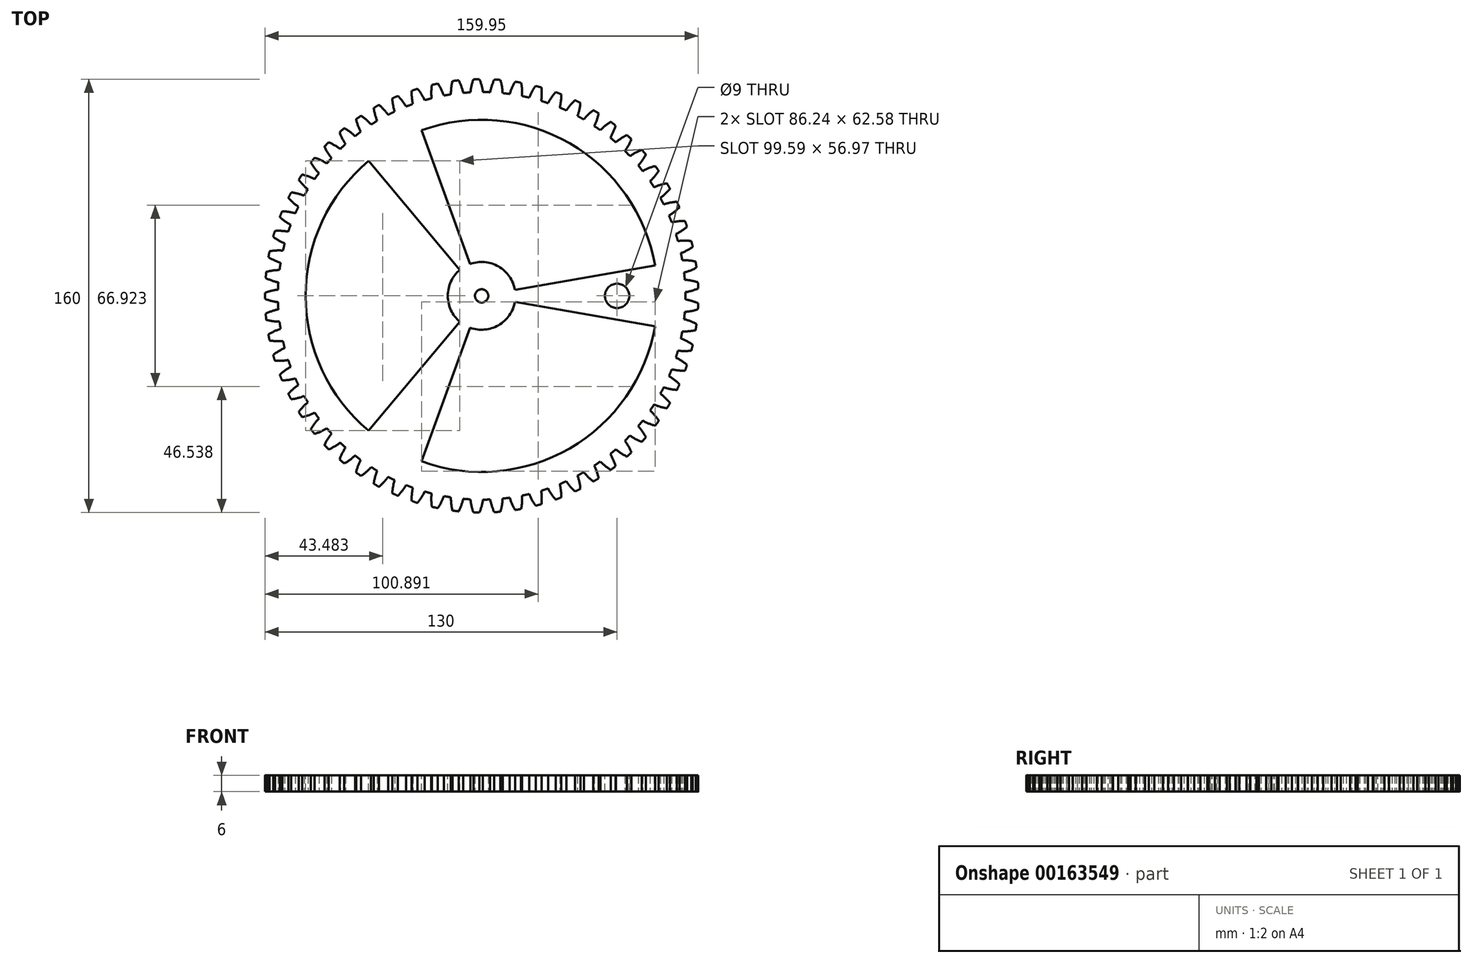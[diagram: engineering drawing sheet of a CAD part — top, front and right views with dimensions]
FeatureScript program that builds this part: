
annotation { "Feature Type Name" : "Feature", "Feature Type Description" : "" }
export const myFeature = defineFeature(function(context is Context, id is Id, definition is map)
    precondition{}
    {
        {
            var Q0;
            Q0=qCreatedBy(makeId("Top.planeOp"),FACE);
            var sketch = newSketch(context, id + "F0", { "sketchPlane" : qUnion([Q0])});
            skCircle(sketch, "E0", {"center": v(0, 0) * mm, "radius": 75.22 * mm, "construction": true});
            skCircle(sketch, "E1", {"center": v(0, 0) * mm, "radius": 77.61 * mm, "construction": true});
            skCircle(sketch, "E2", {"center": v(0, 0) * mm, "radius": 80 * mm, "construction": true});
            skLineSegment(sketch, "E3", {"start": v(0, 0) * mm, "end": v(0, 21.75) * mm, "construction": true});
            skLineSegment(sketch, "E4", {"start": v(0, 0) * mm, "end": v(-0.52, 21.72) * mm, "construction": true});
            skLineSegment(sketch, "E5", {"start": v(0, 77.61) * mm, "end": v(-10.54, 77.61) * mm, "construction": true});
            skLineSegment(sketch, "E6", {"start": v(0, 77.61) * mm, "end": v(-24.6, 71.02) * mm, "construction": true});
            skCircle(sketch, "E7", {"center": v(0, 77.61) * mm, "radius": 19.4 * mm, "construction": true});
            skCircle(sketch, "E8", {"center": v(-18.74, 72.6) * mm, "radius": 19.4 * mm, "construction": true});
            skArc(sketch, "E9", {"start": v(-37.48, 77.61) * mm, "mid": v(-38.1, 74.03) * mm, "end": v(-38.02, 70.39) * mm});
            skPoint(sketch, "E10.center", {"position": v(4.35, 4.65) * mm});
            skCircle(sketch, "E11", {"center": v(0, 0) * mm, "radius": 2.45 * mm});
            skArc(sketch, "E12", {"start": v(0.48, 75.22) * mm, "mid": v(-0.01, 77.65) * mm, "end": v(-0.8, 80) * mm});
            skArc(sketch, "E13.MirrorCS", {"start": v(-4.12, 75.11) * mm, "mid": v(-3.74, 77.56) * mm, "end": v(-3.06, 79.94) * mm});
            skArc(sketch, "E14", {"start": v(-0.8, 80) * mm, "mid": v(-1.93, 79.98) * mm, "end": v(-3.06, 79.94) * mm});
            skArc(sketch, "E15.1.0", {"start": v(-8.52, 79.54) * mm, "mid": v(-9.64, 79.42) * mm, "end": v(-10.76, 79.27) * mm});
            skArc(sketch, "E15.1.1", {"start": v(-6.78, 74.92) * mm, "mid": v(-7.5, 77.29) * mm, "end": v(-8.52, 79.54) * mm});
            skArc(sketch, "E15.1.2", {"start": v(-11.35, 74.36) * mm, "mid": v(-11.2, 76.84) * mm, "end": v(-10.76, 79.27) * mm});
            skArc(sketch, "E15.2.0", {"start": v(-16.16, 78.35) * mm, "mid": v(-17.26, 78.12) * mm, "end": v(-18.36, 77.86) * mm});
            skArc(sketch, "E15.2.1", {"start": v(-13.98, 73.91) * mm, "mid": v(-14.93, 76.2) * mm, "end": v(-16.16, 78.35) * mm});
            skArc(sketch, "E15.2.2", {"start": v(-18.47, 72.92) * mm, "mid": v(-18.57, 75.4) * mm, "end": v(-18.36, 77.86) * mm});
            skArc(sketch, "E15.3.0", {"start": v(-23.65, 76.42) * mm, "mid": v(-24.72, 76.08) * mm, "end": v(-25.79, 75.73) * mm});
            skArc(sketch, "E15.3.1", {"start": v(-21.05, 72.22) * mm, "mid": v(-22.21, 74.4) * mm, "end": v(-23.65, 76.42) * mm});
            skArc(sketch, "E15.3.2", {"start": v(-25.42, 70.8) * mm, "mid": v(-25.76, 73.25) * mm, "end": v(-25.79, 75.73) * mm});
            skArc(sketch, "E15.4.0", {"start": v(-30.91, 73.79) * mm, "mid": v(-31.95, 73.34) * mm, "end": v(-32.98, 72.89) * mm});
            skArc(sketch, "E15.4.1", {"start": v(-27.92, 69.85) * mm, "mid": v(-29.3, 71.91) * mm, "end": v(-30.91, 73.79) * mm});
            skArc(sketch, "E15.4.2", {"start": v(-32.14, 68.01) * mm, "mid": v(-32.71, 70.42) * mm, "end": v(-32.98, 72.89) * mm});
            skArc(sketch, "E15.5.0", {"start": v(-37.9, 70.46) * mm, "mid": v(-38.88, 69.92) * mm, "end": v(-39.86, 69.36) * mm});
            skArc(sketch, "E15.5.1", {"start": v(-34.53, 66.83) * mm, "mid": v(-36.1, 68.75) * mm, "end": v(-37.9, 70.46) * mm});
            skArc(sketch, "E15.5.2", {"start": v(-38.55, 64.6) * mm, "mid": v(-39.36, 66.94) * mm, "end": v(-39.86, 69.36) * mm});
            skArc(sketch, "E15.6.0", {"start": v(-44.51, 66.47) * mm, "mid": v(-45.45, 65.84) * mm, "end": v(-46.37, 65.2) * mm});
            skArc(sketch, "E15.6.1", {"start": v(-40.82, 63.19) * mm, "mid": v(-42.56, 64.95) * mm, "end": v(-44.51, 66.47) * mm});
            skArc(sketch, "E15.6.2", {"start": v(-44.6, 60.57) * mm, "mid": v(-45.63, 62.83) * mm, "end": v(-46.37, 65.2) * mm});
            skArc(sketch, "E15.7.0", {"start": v(-50.72, 61.86) * mm, "mid": v(-51.59, 61.15) * mm, "end": v(-52.44, 60.41) * mm});
            skArc(sketch, "E15.7.1", {"start": v(-46.73, 58.95) * mm, "mid": v(-48.63, 60.54) * mm, "end": v(-50.72, 61.86) * mm});
            skArc(sketch, "E15.7.2", {"start": v(-50.24, 55.99) * mm, "mid": v(-51.48, 58.13) * mm, "end": v(-52.44, 60.41) * mm});
            skArc(sketch, "E15.8.0", {"start": v(-56.46, 56.68) * mm, "mid": v(-57.25, 55.88) * mm, "end": v(-58.03, 55.07) * mm});
            skArc(sketch, "E15.8.1", {"start": v(-52.2, 54.17) * mm, "mid": v(-54.25, 55.56) * mm, "end": v(-56.46, 56.68) * mm});
            skArc(sketch, "E15.8.2", {"start": v(-55.41, 50.87) * mm, "mid": v(-56.85, 52.89) * mm, "end": v(-58.03, 55.07) * mm});
            skArc(sketch, "E15.9.0", {"start": v(-61.66, 50.97) * mm, "mid": v(-62.37, 50.1) * mm, "end": v(-63.07, 49.21) * mm});
            skArc(sketch, "E15.9.1", {"start": v(-57.18, 48.87) * mm, "mid": v(-59.36, 50.06) * mm, "end": v(-61.66, 50.97) * mm});
            skArc(sketch, "E15.9.2", {"start": v(-60.06, 45.29) * mm, "mid": v(-61.7, 47.15) * mm, "end": v(-63.07, 49.21) * mm});
            skArc(sketch, "E15.10.0", {"start": v(-66.3, 44.78) * mm, "mid": v(-66.92, 43.84) * mm, "end": v(-67.53, 42.9) * mm});
            skArc(sketch, "E15.10.1", {"start": v(-61.63, 43.13) * mm, "mid": v(-63.91, 44.1) * mm, "end": v(-66.3, 44.78) * mm});
            skArc(sketch, "E15.10.2", {"start": v(-64.15, 39.28) * mm, "mid": v(-65.96, 40.98) * mm, "end": v(-67.53, 42.9) * mm});
            skArc(sketch, "E15.11.0", {"start": v(-70.3, 38.17) * mm, "mid": v(-70.84, 37.18) * mm, "end": v(-71.35, 36.18) * mm});
            skArc(sketch, "E15.11.1", {"start": v(-65.5, 36.98) * mm, "mid": v(-67.87, 37.73) * mm, "end": v(-70.3, 38.17) * mm});
            skArc(sketch, "E15.11.2", {"start": v(-67.64, 32.9) * mm, "mid": v(-69.6, 34.42) * mm, "end": v(-71.35, 36.18) * mm});
            skArc(sketch, "E15.12.0", {"start": v(-73.66, 31.2) * mm, "mid": v(-74.1, 30.17) * mm, "end": v(-74.51, 29.12) * mm});
            skArc(sketch, "E15.12.1", {"start": v(-68.77, 30.48) * mm, "mid": v(-71.2, 31) * mm, "end": v(-73.66, 31.2) * mm});
            skArc(sketch, "E15.12.2", {"start": v(-70.5, 26.22) * mm, "mid": v(-72.6, 27.54) * mm, "end": v(-74.51, 29.12) * mm});
            skArc(sketch, "E15.13.0", {"start": v(-76.33, 23.95) * mm, "mid": v(-76.66, 22.88) * mm, "end": v(-76.97, 21.8) * mm});
            skArc(sketch, "E15.13.1", {"start": v(-71.4, 23.7) * mm, "mid": v(-73.85, 23.99) * mm, "end": v(-76.33, 23.95) * mm});
            skArc(sketch, "E15.13.2", {"start": v(-72.7, 19.3) * mm, "mid": v(-74.92, 20.4) * mm, "end": v(-76.97, 21.8) * mm});
            skArc(sketch, "E15.14.0", {"start": v(-78.29, 16.47) * mm, "mid": v(-78.5, 15.37) * mm, "end": v(-78.72, 14.26) * mm});
            skArc(sketch, "E15.14.1", {"start": v(-73.35, 16.7) * mm, "mid": v(-75.82, 16.75) * mm, "end": v(-78.29, 16.47) * mm});
            skArc(sketch, "E15.14.2", {"start": v(-74.23, 12.19) * mm, "mid": v(-76.54, 13.08) * mm, "end": v(-78.72, 14.26) * mm});
            skArc(sketch, "E15.15.0", {"start": v(-79.51, 8.84) * mm, "mid": v(-79.63, 7.72) * mm, "end": v(-79.73, 6.6) * mm});
            skArc(sketch, "E15.15.1", {"start": v(-74.62, 9.55) * mm, "mid": v(-77.09, 9.35) * mm, "end": v(-79.51, 8.84) * mm});
            skArc(sketch, "E15.15.2", {"start": v(-75.06, 4.97) * mm, "mid": v(-77.45, 5.63) * mm, "end": v(-79.73, 6.6) * mm});
            skArc(sketch, "E15.16.0", {"start": v(-80, 1.13) * mm, "mid": v(-80, 0) * mm, "end": v(-80, -1.13) * mm});
            skArc(sketch, "E15.16.1", {"start": v(-75.19, 2.3) * mm, "mid": v(-77.63, 1.87) * mm, "end": v(-80, 1.13) * mm});
            skArc(sketch, "E15.16.2", {"start": v(-75.19, -2.3) * mm, "mid": v(-77.63, -1.87) * mm, "end": v(-80, -1.13) * mm});
            skArc(sketch, "E15.17.0", {"start": v(-79.73, -6.6) * mm, "mid": v(-79.63, -7.72) * mm, "end": v(-79.51, -8.84) * mm});
            skArc(sketch, "E15.17.1", {"start": v(-75.06, -4.97) * mm, "mid": v(-77.45, -5.63) * mm, "end": v(-79.73, -6.6) * mm});
            skArc(sketch, "E15.17.2", {"start": v(-74.62, -9.55) * mm, "mid": v(-77.09, -9.35) * mm, "end": v(-79.51, -8.84) * mm});
            skArc(sketch, "E15.18.0", {"start": v(-78.72, -14.26) * mm, "mid": v(-78.5, -15.37) * mm, "end": v(-78.29, -16.47) * mm});
            skArc(sketch, "E15.18.1", {"start": v(-74.23, -12.19) * mm, "mid": v(-76.54, -13.08) * mm, "end": v(-78.72, -14.26) * mm});
            skArc(sketch, "E15.18.2", {"start": v(-73.35, -16.7) * mm, "mid": v(-75.82, -16.75) * mm, "end": v(-78.29, -16.47) * mm});
            skArc(sketch, "E15.19.0", {"start": v(-76.97, -21.8) * mm, "mid": v(-76.66, -22.88) * mm, "end": v(-76.33, -23.95) * mm});
            skArc(sketch, "E15.19.1", {"start": v(-72.7, -19.3) * mm, "mid": v(-74.92, -20.4) * mm, "end": v(-76.97, -21.8) * mm});
            skArc(sketch, "E15.19.2", {"start": v(-71.4, -23.7) * mm, "mid": v(-73.85, -23.99) * mm, "end": v(-76.33, -23.95) * mm});
            skArc(sketch, "E15.20.0", {"start": v(-74.51, -29.12) * mm, "mid": v(-74.1, -30.17) * mm, "end": v(-73.66, -31.2) * mm});
            skArc(sketch, "E15.20.1", {"start": v(-70.5, -26.22) * mm, "mid": v(-72.6, -27.54) * mm, "end": v(-74.51, -29.12) * mm});
            skArc(sketch, "E15.20.2", {"start": v(-68.77, -30.48) * mm, "mid": v(-71.2, -31) * mm, "end": v(-73.66, -31.2) * mm});
            skArc(sketch, "E15.21.0", {"start": v(-71.35, -36.18) * mm, "mid": v(-70.84, -37.18) * mm, "end": v(-70.3, -38.17) * mm});
            skArc(sketch, "E15.21.1", {"start": v(-67.64, -32.9) * mm, "mid": v(-69.6, -34.42) * mm, "end": v(-71.35, -36.18) * mm});
            skArc(sketch, "E15.21.2", {"start": v(-65.5, -36.98) * mm, "mid": v(-67.87, -37.73) * mm, "end": v(-70.3, -38.17) * mm});
            skArc(sketch, "E15.22.0", {"start": v(-67.53, -42.9) * mm, "mid": v(-66.92, -43.84) * mm, "end": v(-66.3, -44.78) * mm});
            skArc(sketch, "E15.22.1", {"start": v(-64.15, -39.28) * mm, "mid": v(-65.96, -40.98) * mm, "end": v(-67.53, -42.9) * mm});
            skArc(sketch, "E15.22.2", {"start": v(-61.63, -43.13) * mm, "mid": v(-63.91, -44.1) * mm, "end": v(-66.3, -44.78) * mm});
            skArc(sketch, "E15.23.0", {"start": v(-63.07, -49.21) * mm, "mid": v(-62.37, -50.1) * mm, "end": v(-61.66, -50.97) * mm});
            skArc(sketch, "E15.23.1", {"start": v(-60.06, -45.29) * mm, "mid": v(-61.7, -47.15) * mm, "end": v(-63.07, -49.21) * mm});
            skArc(sketch, "E15.23.2", {"start": v(-57.18, -48.87) * mm, "mid": v(-59.36, -50.06) * mm, "end": v(-61.66, -50.97) * mm});
            skArc(sketch, "E15.24.0", {"start": v(-58.03, -55.07) * mm, "mid": v(-57.25, -55.88) * mm, "end": v(-56.46, -56.68) * mm});
            skArc(sketch, "E15.24.1", {"start": v(-55.41, -50.87) * mm, "mid": v(-56.85, -52.89) * mm, "end": v(-58.03, -55.07) * mm});
            skArc(sketch, "E15.24.2", {"start": v(-52.2, -54.17) * mm, "mid": v(-54.25, -55.56) * mm, "end": v(-56.46, -56.68) * mm});
            skArc(sketch, "E15.25.0", {"start": v(-52.44, -60.41) * mm, "mid": v(-51.59, -61.15) * mm, "end": v(-50.72, -61.86) * mm});
            skArc(sketch, "E15.25.1", {"start": v(-50.24, -55.99) * mm, "mid": v(-51.48, -58.13) * mm, "end": v(-52.44, -60.41) * mm});
            skArc(sketch, "E15.25.2", {"start": v(-46.73, -58.95) * mm, "mid": v(-48.63, -60.54) * mm, "end": v(-50.72, -61.86) * mm});
            skArc(sketch, "E15.26.0", {"start": v(-46.37, -65.2) * mm, "mid": v(-45.45, -65.84) * mm, "end": v(-44.51, -66.47) * mm});
            skArc(sketch, "E15.26.1", {"start": v(-44.6, -60.57) * mm, "mid": v(-45.63, -62.83) * mm, "end": v(-46.37, -65.2) * mm});
            skArc(sketch, "E15.26.2", {"start": v(-40.82, -63.19) * mm, "mid": v(-42.56, -64.95) * mm, "end": v(-44.51, -66.47) * mm});
            skArc(sketch, "E15.27.0", {"start": v(-39.86, -69.36) * mm, "mid": v(-38.88, -69.92) * mm, "end": v(-37.9, -70.46) * mm});
            skArc(sketch, "E15.27.1", {"start": v(-38.55, -64.6) * mm, "mid": v(-39.36, -66.94) * mm, "end": v(-39.86, -69.36) * mm});
            skArc(sketch, "E15.27.2", {"start": v(-34.53, -66.83) * mm, "mid": v(-36.1, -68.75) * mm, "end": v(-37.9, -70.46) * mm});
            skArc(sketch, "E15.28.0", {"start": v(-32.98, -72.89) * mm, "mid": v(-31.95, -73.34) * mm, "end": v(-30.91, -73.79) * mm});
            skArc(sketch, "E15.28.1", {"start": v(-32.14, -68.01) * mm, "mid": v(-32.71, -70.42) * mm, "end": v(-32.98, -72.89) * mm});
            skArc(sketch, "E15.28.2", {"start": v(-27.92, -69.85) * mm, "mid": v(-29.3, -71.91) * mm, "end": v(-30.91, -73.79) * mm});
            skArc(sketch, "E15.29.0", {"start": v(-25.79, -75.73) * mm, "mid": v(-24.72, -76.08) * mm, "end": v(-23.65, -76.42) * mm});
            skArc(sketch, "E15.29.1", {"start": v(-25.42, -70.8) * mm, "mid": v(-25.76, -73.25) * mm, "end": v(-25.79, -75.73) * mm});
            skArc(sketch, "E15.29.2", {"start": v(-21.05, -72.22) * mm, "mid": v(-22.21, -74.4) * mm, "end": v(-23.65, -76.42) * mm});
            skArc(sketch, "E15.30.0", {"start": v(-18.36, -77.86) * mm, "mid": v(-17.26, -78.12) * mm, "end": v(-16.16, -78.35) * mm});
            skArc(sketch, "E15.30.1", {"start": v(-18.47, -72.92) * mm, "mid": v(-18.57, -75.4) * mm, "end": v(-18.36, -77.86) * mm});
            skArc(sketch, "E15.30.2", {"start": v(-13.98, -73.91) * mm, "mid": v(-14.93, -76.2) * mm, "end": v(-16.16, -78.35) * mm});
            skArc(sketch, "E15.31.0", {"start": v(-10.76, -79.27) * mm, "mid": v(-9.64, -79.42) * mm, "end": v(-8.52, -79.54) * mm});
            skArc(sketch, "E15.31.1", {"start": v(-11.35, -74.36) * mm, "mid": v(-11.2, -76.84) * mm, "end": v(-10.76, -79.27) * mm});
            skArc(sketch, "E15.31.2", {"start": v(-6.78, -74.92) * mm, "mid": v(-7.5, -77.29) * mm, "end": v(-8.52, -79.54) * mm});
            skArc(sketch, "E15.32.0", {"start": v(-3.06, -79.94) * mm, "mid": v(-1.93, -79.98) * mm, "end": v(-0.8, -80) * mm});
            skArc(sketch, "E15.32.1", {"start": v(-4.12, -75.11) * mm, "mid": v(-3.74, -77.56) * mm, "end": v(-3.06, -79.94) * mm});
            skArc(sketch, "E15.32.2", {"start": v(0.48, -75.22) * mm, "mid": v(-0.01, -77.65) * mm, "end": v(-0.8, -80) * mm});
            skArc(sketch, "E15.33.0", {"start": v(4.67, -79.86) * mm, "mid": v(5.8, -79.79) * mm, "end": v(6.92, -79.7) * mm});
            skArc(sketch, "E15.33.1", {"start": v(3.15, -75.16) * mm, "mid": v(3.76, -77.56) * mm, "end": v(4.67, -79.86) * mm});
            skArc(sketch, "E15.33.2", {"start": v(7.74, -74.82) * mm, "mid": v(7.48, -77.29) * mm, "end": v(6.92, -79.7) * mm});
            skArc(sketch, "E15.34.0", {"start": v(12.36, -79.04) * mm, "mid": v(13.47, -78.86) * mm, "end": v(14.58, -78.66) * mm});
            skArc(sketch, "E15.34.1", {"start": v(10.4, -74.5) * mm, "mid": v(11.23, -76.83) * mm, "end": v(12.36, -79.04) * mm});
            skArc(sketch, "E15.34.2", {"start": v(14.93, -73.73) * mm, "mid": v(14.9, -76.2) * mm, "end": v(14.58, -78.66) * mm});
            skArc(sketch, "E15.35.0", {"start": v(19.93, -77.48) * mm, "mid": v(21.02, -77.2) * mm, "end": v(22.1, -76.89) * mm});
            skArc(sketch, "E15.35.1", {"start": v(17.53, -73.15) * mm, "mid": v(18.6, -75.4) * mm, "end": v(19.93, -77.48) * mm});
            skArc(sketch, "E15.35.2", {"start": v(21.97, -71.94) * mm, "mid": v(22.2, -74.41) * mm, "end": v(22.1, -76.89) * mm});
            skArc(sketch, "E15.36.0", {"start": v(27.31, -75.2) * mm, "mid": v(28.37, -74.8) * mm, "end": v(29.42, -74.4) * mm});
            skArc(sketch, "E15.36.1", {"start": v(24.51, -71.12) * mm, "mid": v(25.78, -73.25) * mm, "end": v(27.31, -75.2) * mm});
            skArc(sketch, "E15.36.2", {"start": v(28.81, -69.49) * mm, "mid": v(29.27, -71.92) * mm, "end": v(29.42, -74.4) * mm});
            skArc(sketch, "E15.37.0", {"start": v(34.44, -72.2) * mm, "mid": v(35.46, -71.71) * mm, "end": v(36.46, -71.2) * mm});
            skArc(sketch, "E15.37.1", {"start": v(31.26, -68.42) * mm, "mid": v(32.73, -70.41) * mm, "end": v(34.44, -72.2) * mm});
            skArc(sketch, "E15.37.2", {"start": v(35.38, -66.38) * mm, "mid": v(36.08, -68.76) * mm, "end": v(36.46, -71.2) * mm});
            skArc(sketch, "E15.38.0", {"start": v(41.25, -68.54) * mm, "mid": v(42.21, -67.96) * mm, "end": v(43.16, -67.36) * mm});
            skArc(sketch, "E15.38.1", {"start": v(37.72, -65.08) * mm, "mid": v(39.37, -66.93) * mm, "end": v(41.25, -68.54) * mm});
            skArc(sketch, "E15.38.2", {"start": v(41.63, -62.66) * mm, "mid": v(42.54, -64.96) * mm, "end": v(43.16, -67.36) * mm});
            skArc(sketch, "E15.39.0", {"start": v(47.67, -64.24) * mm, "mid": v(48.57, -63.57) * mm, "end": v(49.46, -62.88) * mm});
            skArc(sketch, "E15.39.1", {"start": v(43.82, -61.14) * mm, "mid": v(45.65, -62.81) * mm, "end": v(47.67, -64.24) * mm});
            skArc(sketch, "E15.39.2", {"start": v(47.48, -58.35) * mm, "mid": v(48.62, -60.55) * mm, "end": v(49.46, -62.88) * mm});
            skArc(sketch, "E15.40.0", {"start": v(53.65, -59.34) * mm, "mid": v(54.48, -58.58) * mm, "end": v(55.3, -57.8) * mm});
            skArc(sketch, "E15.40.1", {"start": v(49.52, -56.62) * mm, "mid": v(51.5, -58.12) * mm, "end": v(53.65, -59.34) * mm});
            skArc(sketch, "E15.40.2", {"start": v(52.89, -53.5) * mm, "mid": v(54.23, -55.57) * mm, "end": v(55.3, -57.8) * mm});
            skArc(sketch, "E15.41.0", {"start": v(59.13, -53.89) * mm, "mid": v(59.88, -53.05) * mm, "end": v(60.62, -52.2) * mm});
            skArc(sketch, "E15.41.1", {"start": v(54.75, -51.58) * mm, "mid": v(56.87, -52.87) * mm, "end": v(59.13, -53.89) * mm});
            skArc(sketch, "E15.41.2", {"start": v(57.8, -48.14) * mm, "mid": v(59.34, -50.08) * mm, "end": v(60.62, -52.2) * mm});
            skArc(sketch, "E15.42.0", {"start": v(64.05, -47.93) * mm, "mid": v(64.72, -47.02) * mm, "end": v(65.38, -46.1) * mm});
            skArc(sketch, "E15.42.1", {"start": v(59.48, -46.05) * mm, "mid": v(61.7, -47.14) * mm, "end": v(64.05, -47.93) * mm});
            skArc(sketch, "E15.42.2", {"start": v(62.18, -42.33) * mm, "mid": v(63.9, -44.12) * mm, "end": v(65.38, -46.1) * mm});
            skArc(sketch, "E15.43.0", {"start": v(68.38, -41.52) * mm, "mid": v(68.96, -40.56) * mm, "end": v(69.52, -39.58) * mm});
            skArc(sketch, "E15.43.1", {"start": v(63.64, -40.1) * mm, "mid": v(65.97, -40.96) * mm, "end": v(68.38, -41.52) * mm});
            skArc(sketch, "E15.43.2", {"start": v(65.98, -36.14) * mm, "mid": v(67.86, -37.75) * mm, "end": v(69.52, -39.58) * mm});
            skArc(sketch, "E15.44.0", {"start": v(72.07, -34.73) * mm, "mid": v(72.55, -33.71) * mm, "end": v(73.02, -32.69) * mm});
            skArc(sketch, "E15.44.1", {"start": v(67.22, -33.77) * mm, "mid": v(69.61, -34.4) * mm, "end": v(72.07, -34.73) * mm});
            skArc(sketch, "E15.44.2", {"start": v(69.16, -29.6) * mm, "mid": v(71.19, -31.02) * mm, "end": v(73.02, -32.69) * mm});
            skArc(sketch, "E15.45.0", {"start": v(75.08, -27.61) * mm, "mid": v(75.46, -26.55) * mm, "end": v(75.83, -25.49) * mm});
            skArc(sketch, "E15.45.1", {"start": v(70.16, -27.12) * mm, "mid": v(72.6, -27.53) * mm, "end": v(75.08, -27.61) * mm});
            skArc(sketch, "E15.45.2", {"start": v(71.69, -22.79) * mm, "mid": v(73.85, -24) * mm, "end": v(75.83, -25.49) * mm});
            skArc(sketch, "E15.46.0", {"start": v(77.4, -20.24) * mm, "mid": v(77.68, -19.15) * mm, "end": v(77.94, -18.05) * mm});
            skArc(sketch, "E15.46.1", {"start": v(72.45, -20.23) * mm, "mid": v(74.93, -20.39) * mm, "end": v(77.4, -20.24) * mm});
            skArc(sketch, "E15.46.2", {"start": v(73.55, -15.76) * mm, "mid": v(75.82, -16.77) * mm, "end": v(77.94, -18.05) * mm});
            skArc(sketch, "E15.47.0", {"start": v(79, -12.67) * mm, "mid": v(79.16, -11.56) * mm, "end": v(79.32, -10.44) * mm});
            skArc(sketch, "E15.47.1", {"start": v(74.07, -13.14) * mm, "mid": v(76.54, -13.06) * mm, "end": v(79, -12.67) * mm});
            skArc(sketch, "E15.47.2", {"start": v(74.73, -8.59) * mm, "mid": v(77.08, -9.37) * mm, "end": v(79.32, -10.44) * mm});
            skArc(sketch, "E16.4.48.0", {"start": v(74.99, -5.93) * mm, "mid": v(77.45, -5.61) * mm, "end": v(79.84, -4.99) * mm});
            skArc(sketch, "E16.8.48.0", {"start": v(75.21, -1.34) * mm, "mid": v(77.63, -1.89) * mm, "end": v(79.95, -2.74) * mm});
            skArc(sketch, "E16.10.48.0", {"start": v(79.84, -4.99) * mm, "mid": v(79.9, -3.87) * mm, "end": v(79.95, -2.74) * mm});
            skArc(sketch, "E16.4.49.0", {"start": v(75.21, 1.34) * mm, "mid": v(77.63, 1.89) * mm, "end": v(79.95, 2.74) * mm});
            skArc(sketch, "E16.8.49.0", {"start": v(74.99, 5.93) * mm, "mid": v(77.45, 5.61) * mm, "end": v(79.84, 4.99) * mm});
            skArc(sketch, "E16.10.49.0", {"start": v(79.95, 2.74) * mm, "mid": v(79.9, 3.87) * mm, "end": v(79.84, 4.99) * mm});
            skArc(sketch, "E17", {"start": v(3.15, 75.16) * mm, "mid": v(1.82, 75.2) * mm, "end": v(0.48, 75.22) * mm});
            skArc(sketch, "E18.1.0", {"start": v(-4.12, 75.11) * mm, "mid": v(-5.45, 75.03) * mm, "end": v(-6.78, 74.92) * mm});
            skArc(sketch, "E18.2.0", {"start": v(-11.35, 74.36) * mm, "mid": v(-12.66, 74.15) * mm, "end": v(-13.98, 73.91) * mm});
            skArc(sketch, "E18.3.0", {"start": v(-18.47, 72.92) * mm, "mid": v(-19.76, 72.58) * mm, "end": v(-21.05, 72.22) * mm});
            skArc(sketch, "E18.4.0", {"start": v(-25.42, 70.8) * mm, "mid": v(-26.67, 70.34) * mm, "end": v(-27.92, 69.85) * mm});
            skArc(sketch, "E18.5.0", {"start": v(-32.14, 68.01) * mm, "mid": v(-33.34, 67.43) * mm, "end": v(-34.53, 66.83) * mm});
            skArc(sketch, "E18.6.0", {"start": v(-38.55, 64.6) * mm, "mid": v(-39.7, 63.9) * mm, "end": v(-40.82, 63.19) * mm});
            skArc(sketch, "E18.7.0", {"start": v(-44.6, 60.57) * mm, "mid": v(-45.67, 59.77) * mm, "end": v(-46.73, 58.95) * mm});
            skArc(sketch, "E18.8.0", {"start": v(-50.24, 55.99) * mm, "mid": v(-51.23, 55.08) * mm, "end": v(-52.2, 54.17) * mm});
            skArc(sketch, "E18.9.0", {"start": v(-55.41, 50.87) * mm, "mid": v(-56.3, 49.88) * mm, "end": v(-57.18, 48.87) * mm});
            skArc(sketch, "E18.10.0", {"start": v(-60.06, 45.29) * mm, "mid": v(-60.86, 44.22) * mm, "end": v(-61.63, 43.13) * mm});
            skArc(sketch, "E18.11.0", {"start": v(-64.15, 39.28) * mm, "mid": v(-64.84, 38.14) * mm, "end": v(-65.5, 36.98) * mm});
            skArc(sketch, "E18.12.0", {"start": v(-67.64, 32.9) * mm, "mid": v(-68.22, 31.7) * mm, "end": v(-68.77, 30.48) * mm});
            skArc(sketch, "E18.13.0", {"start": v(-70.5, 26.22) * mm, "mid": v(-70.96, 24.97) * mm, "end": v(-71.4, 23.7) * mm});
            skArc(sketch, "E18.14.0", {"start": v(-72.7, 19.3) * mm, "mid": v(-73.04, 18) * mm, "end": v(-73.35, 16.7) * mm});
            skArc(sketch, "E18.15.0", {"start": v(-74.23, 12.19) * mm, "mid": v(-74.43, 10.87) * mm, "end": v(-74.62, 9.55) * mm});
            skArc(sketch, "E18.16.0", {"start": v(-75.06, 4.97) * mm, "mid": v(-75.14, 3.63) * mm, "end": v(-75.19, 2.3) * mm});
            skArc(sketch, "E18.17.0", {"start": v(-75.19, -2.3) * mm, "mid": v(-75.14, -3.63) * mm, "end": v(-75.06, -4.97) * mm});
            skArc(sketch, "E18.18.0", {"start": v(-74.62, -9.55) * mm, "mid": v(-74.43, -10.87) * mm, "end": v(-74.23, -12.19) * mm});
            skArc(sketch, "E18.19.0", {"start": v(-73.35, -16.7) * mm, "mid": v(-73.04, -18) * mm, "end": v(-72.7, -19.3) * mm});
            skArc(sketch, "E18.20.0", {"start": v(-71.4, -23.7) * mm, "mid": v(-70.96, -24.97) * mm, "end": v(-70.5, -26.22) * mm});
            skArc(sketch, "E18.21.0", {"start": v(-68.77, -30.48) * mm, "mid": v(-68.22, -31.7) * mm, "end": v(-67.64, -32.9) * mm});
            skArc(sketch, "E18.22.0", {"start": v(-65.5, -36.98) * mm, "mid": v(-64.84, -38.14) * mm, "end": v(-64.15, -39.28) * mm});
            skArc(sketch, "E18.23.0", {"start": v(-61.63, -43.13) * mm, "mid": v(-60.86, -44.22) * mm, "end": v(-60.06, -45.29) * mm});
            skArc(sketch, "E18.24.0", {"start": v(-57.18, -48.87) * mm, "mid": v(-56.3, -49.88) * mm, "end": v(-55.41, -50.87) * mm});
            skArc(sketch, "E18.25.0", {"start": v(-52.2, -54.17) * mm, "mid": v(-51.23, -55.08) * mm, "end": v(-50.24, -55.99) * mm});
            skArc(sketch, "E18.26.0", {"start": v(-46.73, -58.95) * mm, "mid": v(-45.67, -59.77) * mm, "end": v(-44.6, -60.57) * mm});
            skArc(sketch, "E18.27.0", {"start": v(-40.82, -63.19) * mm, "mid": v(-39.7, -63.9) * mm, "end": v(-38.55, -64.6) * mm});
            skArc(sketch, "E18.28.0", {"start": v(-34.53, -66.83) * mm, "mid": v(-33.34, -67.43) * mm, "end": v(-32.14, -68.01) * mm});
            skArc(sketch, "E18.29.0", {"start": v(-27.92, -69.85) * mm, "mid": v(-26.67, -70.34) * mm, "end": v(-25.42, -70.8) * mm});
            skArc(sketch, "E18.30.0", {"start": v(-21.05, -72.22) * mm, "mid": v(-19.76, -72.58) * mm, "end": v(-18.47, -72.92) * mm});
            skArc(sketch, "E18.31.0", {"start": v(-13.98, -73.91) * mm, "mid": v(-12.66, -74.15) * mm, "end": v(-11.35, -74.36) * mm});
            skArc(sketch, "E18.32.0", {"start": v(-6.78, -74.92) * mm, "mid": v(-5.45, -75.03) * mm, "end": v(-4.12, -75.11) * mm});
            skArc(sketch, "E18.33.0", {"start": v(0.48, -75.22) * mm, "mid": v(1.82, -75.2) * mm, "end": v(3.15, -75.16) * mm});
            skArc(sketch, "E18.34.0", {"start": v(7.74, -74.82) * mm, "mid": v(9.07, -74.68) * mm, "end": v(10.4, -74.5) * mm});
            skArc(sketch, "E18.35.0", {"start": v(14.93, -73.73) * mm, "mid": v(16.23, -73.45) * mm, "end": v(17.53, -73.15) * mm});
            skArc(sketch, "E18.36.0", {"start": v(21.97, -71.94) * mm, "mid": v(23.25, -71.54) * mm, "end": v(24.51, -71.12) * mm});
            skArc(sketch, "E18.37.0", {"start": v(28.81, -69.49) * mm, "mid": v(30.04, -68.96) * mm, "end": v(31.26, -68.42) * mm});
            skArc(sketch, "E18.38.0", {"start": v(35.38, -66.38) * mm, "mid": v(36.56, -65.74) * mm, "end": v(37.72, -65.08) * mm});
            skArc(sketch, "E18.39.0", {"start": v(41.63, -62.66) * mm, "mid": v(42.73, -61.9) * mm, "end": v(43.82, -61.14) * mm});
            skArc(sketch, "E18.40.0", {"start": v(47.48, -58.35) * mm, "mid": v(48.5, -57.5) * mm, "end": v(49.52, -56.62) * mm});
            skArc(sketch, "E18.41.0", {"start": v(52.89, -53.5) * mm, "mid": v(53.83, -52.54) * mm, "end": v(54.75, -51.58) * mm});
            skArc(sketch, "E18.42.0", {"start": v(57.8, -48.14) * mm, "mid": v(58.65, -47.1) * mm, "end": v(59.48, -46.05) * mm});
            skArc(sketch, "E18.43.0", {"start": v(62.18, -42.33) * mm, "mid": v(62.92, -41.22) * mm, "end": v(63.64, -40.1) * mm});
            skArc(sketch, "E18.44.0", {"start": v(65.98, -36.14) * mm, "mid": v(66.6, -34.96) * mm, "end": v(67.22, -33.77) * mm});
            skArc(sketch, "E18.45.0", {"start": v(69.16, -29.6) * mm, "mid": v(69.67, -28.37) * mm, "end": v(70.16, -27.12) * mm});
            skArc(sketch, "E18.46.0", {"start": v(71.69, -22.79) * mm, "mid": v(72.08, -21.5) * mm, "end": v(72.45, -20.23) * mm});
            skArc(sketch, "E18.47.0", {"start": v(73.55, -15.76) * mm, "mid": v(73.82, -14.45) * mm, "end": v(74.07, -13.14) * mm});
            skArc(sketch, "E18.48.0", {"start": v(74.73, -8.59) * mm, "mid": v(74.87, -7.26) * mm, "end": v(74.99, -5.93) * mm});
            skArc(sketch, "E18.49.0", {"start": v(75.21, -1.34) * mm, "mid": v(75.22, 0) * mm, "end": v(75.21, 1.34) * mm});
            skArc(sketch, "E19.4.50.0", {"start": v(74.73, 8.59) * mm, "mid": v(77.08, 9.37) * mm, "end": v(79.32, 10.44) * mm});
            skArc(sketch, "E19.8.50.0", {"start": v(74.07, 13.14) * mm, "mid": v(76.54, 13.06) * mm, "end": v(79, 12.67) * mm});
            skArc(sketch, "E19.10.50.0", {"start": v(79.32, 10.44) * mm, "mid": v(79.16, 11.56) * mm, "end": v(79, 12.67) * mm});
            skArc(sketch, "E20.3.50.0", {"start": v(74.99, 5.93) * mm, "mid": v(74.87, 7.26) * mm, "end": v(74.73, 8.59) * mm});
            skArc(sketch, "E21.4.51.0", {"start": v(73.55, 15.76) * mm, "mid": v(75.82, 16.77) * mm, "end": v(77.94, 18.05) * mm});
            skArc(sketch, "E21.8.51.0", {"start": v(72.45, 20.23) * mm, "mid": v(74.93, 20.39) * mm, "end": v(77.4, 20.24) * mm});
            skArc(sketch, "E21.10.51.0", {"start": v(77.94, 18.05) * mm, "mid": v(77.68, 19.15) * mm, "end": v(77.4, 20.24) * mm});
            skArc(sketch, "E21.4.52.0", {"start": v(71.69, 22.79) * mm, "mid": v(73.85, 24) * mm, "end": v(75.83, 25.49) * mm});
            skArc(sketch, "E21.8.52.0", {"start": v(70.16, 27.12) * mm, "mid": v(72.6, 27.53) * mm, "end": v(75.08, 27.61) * mm});
            skArc(sketch, "E21.10.52.0", {"start": v(75.83, 25.49) * mm, "mid": v(75.46, 26.55) * mm, "end": v(75.08, 27.61) * mm});
            skArc(sketch, "E21.4.53.0", {"start": v(69.16, 29.6) * mm, "mid": v(71.19, 31.02) * mm, "end": v(73.02, 32.69) * mm});
            skArc(sketch, "E21.8.53.0", {"start": v(67.22, 33.77) * mm, "mid": v(69.61, 34.4) * mm, "end": v(72.07, 34.73) * mm});
            skArc(sketch, "E21.10.53.0", {"start": v(73.02, 32.69) * mm, "mid": v(72.55, 33.71) * mm, "end": v(72.07, 34.73) * mm});
            skArc(sketch, "E21.4.54.0", {"start": v(65.98, 36.14) * mm, "mid": v(67.86, 37.75) * mm, "end": v(69.52, 39.58) * mm});
            skArc(sketch, "E21.8.54.0", {"start": v(63.64, 40.1) * mm, "mid": v(65.97, 40.96) * mm, "end": v(68.38, 41.52) * mm});
            skArc(sketch, "E21.10.54.0", {"start": v(69.52, 39.58) * mm, "mid": v(68.96, 40.56) * mm, "end": v(68.38, 41.52) * mm});
            skArc(sketch, "E21.4.55.0", {"start": v(62.18, 42.33) * mm, "mid": v(63.9, 44.12) * mm, "end": v(65.38, 46.1) * mm});
            skArc(sketch, "E21.8.55.0", {"start": v(59.48, 46.05) * mm, "mid": v(61.7, 47.14) * mm, "end": v(64.05, 47.93) * mm});
            skArc(sketch, "E21.10.55.0", {"start": v(65.38, 46.1) * mm, "mid": v(64.72, 47.02) * mm, "end": v(64.05, 47.93) * mm});
            skArc(sketch, "E21.4.56.0", {"start": v(57.8, 48.14) * mm, "mid": v(59.34, 50.08) * mm, "end": v(60.62, 52.2) * mm});
            skArc(sketch, "E21.8.56.0", {"start": v(54.75, 51.58) * mm, "mid": v(56.87, 52.87) * mm, "end": v(59.13, 53.89) * mm});
            skArc(sketch, "E21.10.56.0", {"start": v(60.62, 52.2) * mm, "mid": v(59.88, 53.05) * mm, "end": v(59.13, 53.89) * mm});
            skArc(sketch, "E21.4.57.0", {"start": v(52.89, 53.5) * mm, "mid": v(54.23, 55.57) * mm, "end": v(55.3, 57.8) * mm});
            skArc(sketch, "E21.8.57.0", {"start": v(49.52, 56.62) * mm, "mid": v(51.5, 58.12) * mm, "end": v(53.65, 59.34) * mm});
            skArc(sketch, "E21.10.57.0", {"start": v(55.3, 57.8) * mm, "mid": v(54.48, 58.58) * mm, "end": v(53.65, 59.34) * mm});
            skArc(sketch, "E21.4.58.0", {"start": v(47.48, 58.35) * mm, "mid": v(48.62, 60.55) * mm, "end": v(49.46, 62.88) * mm});
            skArc(sketch, "E21.8.58.0", {"start": v(43.82, 61.14) * mm, "mid": v(45.65, 62.81) * mm, "end": v(47.67, 64.24) * mm});
            skArc(sketch, "E21.10.58.0", {"start": v(49.46, 62.88) * mm, "mid": v(48.57, 63.57) * mm, "end": v(47.67, 64.24) * mm});
            skArc(sketch, "E21.4.59.0", {"start": v(41.63, 62.66) * mm, "mid": v(42.54, 64.96) * mm, "end": v(43.16, 67.36) * mm});
            skArc(sketch, "E21.8.59.0", {"start": v(37.72, 65.08) * mm, "mid": v(39.37, 66.93) * mm, "end": v(41.25, 68.54) * mm});
            skArc(sketch, "E21.10.59.0", {"start": v(43.16, 67.36) * mm, "mid": v(42.21, 67.96) * mm, "end": v(41.25, 68.54) * mm});
            skArc(sketch, "E21.4.60.0", {"start": v(35.38, 66.38) * mm, "mid": v(36.08, 68.76) * mm, "end": v(36.46, 71.2) * mm});
            skArc(sketch, "E21.8.60.0", {"start": v(31.26, 68.42) * mm, "mid": v(32.73, 70.41) * mm, "end": v(34.44, 72.2) * mm});
            skArc(sketch, "E21.10.60.0", {"start": v(36.46, 71.2) * mm, "mid": v(35.46, 71.71) * mm, "end": v(34.44, 72.2) * mm});
            skArc(sketch, "E21.4.61.0", {"start": v(28.81, 69.49) * mm, "mid": v(29.27, 71.92) * mm, "end": v(29.42, 74.4) * mm});
            skArc(sketch, "E21.8.61.0", {"start": v(24.51, 71.12) * mm, "mid": v(25.78, 73.25) * mm, "end": v(27.31, 75.2) * mm});
            skArc(sketch, "E21.10.61.0", {"start": v(29.42, 74.4) * mm, "mid": v(28.37, 74.8) * mm, "end": v(27.31, 75.2) * mm});
            skArc(sketch, "E21.4.62.0", {"start": v(21.97, 71.94) * mm, "mid": v(22.2, 74.41) * mm, "end": v(22.1, 76.89) * mm});
            skArc(sketch, "E21.8.62.0", {"start": v(17.53, 73.15) * mm, "mid": v(18.6, 75.4) * mm, "end": v(19.93, 77.48) * mm});
            skArc(sketch, "E21.10.62.0", {"start": v(22.1, 76.89) * mm, "mid": v(21.02, 77.2) * mm, "end": v(19.93, 77.48) * mm});
            skArc(sketch, "E21.4.63.0", {"start": v(14.93, 73.73) * mm, "mid": v(14.9, 76.2) * mm, "end": v(14.58, 78.66) * mm});
            skArc(sketch, "E21.8.63.0", {"start": v(10.4, 74.5) * mm, "mid": v(11.23, 76.83) * mm, "end": v(12.36, 79.04) * mm});
            skArc(sketch, "E21.10.63.0", {"start": v(14.58, 78.66) * mm, "mid": v(13.47, 78.86) * mm, "end": v(12.36, 79.04) * mm});
            skArc(sketch, "E21.4.64.0", {"start": v(7.74, 74.82) * mm, "mid": v(7.48, 77.29) * mm, "end": v(6.92, 79.7) * mm});
            skArc(sketch, "E21.8.64.0", {"start": v(3.15, 75.16) * mm, "mid": v(3.76, 77.56) * mm, "end": v(4.67, 79.86) * mm});
            skArc(sketch, "E21.10.64.0", {"start": v(6.92, 79.7) * mm, "mid": v(5.8, 79.79) * mm, "end": v(4.67, 79.86) * mm});
            skArc(sketch, "E22.3.51.0", {"start": v(74.07, 13.14) * mm, "mid": v(73.82, 14.45) * mm, "end": v(73.55, 15.76) * mm});
            skArc(sketch, "E22.3.52.0", {"start": v(72.45, 20.23) * mm, "mid": v(72.08, 21.5) * mm, "end": v(71.69, 22.79) * mm});
            skArc(sketch, "E22.3.53.0", {"start": v(70.16, 27.12) * mm, "mid": v(69.67, 28.37) * mm, "end": v(69.16, 29.6) * mm});
            skArc(sketch, "E22.3.54.0", {"start": v(67.22, 33.77) * mm, "mid": v(66.6, 34.96) * mm, "end": v(65.98, 36.14) * mm});
            skArc(sketch, "E22.3.55.0", {"start": v(63.64, 40.1) * mm, "mid": v(62.92, 41.22) * mm, "end": v(62.18, 42.33) * mm});
            skArc(sketch, "E22.3.56.0", {"start": v(59.48, 46.05) * mm, "mid": v(58.65, 47.1) * mm, "end": v(57.8, 48.14) * mm});
            skArc(sketch, "E22.3.57.0", {"start": v(54.75, 51.58) * mm, "mid": v(53.83, 52.54) * mm, "end": v(52.89, 53.5) * mm});
            skArc(sketch, "E22.3.58.0", {"start": v(49.52, 56.62) * mm, "mid": v(48.5, 57.5) * mm, "end": v(47.48, 58.35) * mm});
            skArc(sketch, "E22.3.59.0", {"start": v(43.82, 61.14) * mm, "mid": v(42.73, 61.9) * mm, "end": v(41.63, 62.66) * mm});
            skArc(sketch, "E22.3.60.0", {"start": v(37.72, 65.08) * mm, "mid": v(36.56, 65.74) * mm, "end": v(35.38, 66.38) * mm});
            skArc(sketch, "E22.3.61.0", {"start": v(31.26, 68.42) * mm, "mid": v(30.04, 68.96) * mm, "end": v(28.81, 69.49) * mm});
            skArc(sketch, "E22.3.62.0", {"start": v(24.51, 71.12) * mm, "mid": v(23.25, 71.54) * mm, "end": v(21.97, 71.94) * mm});
            skArc(sketch, "E22.3.63.0", {"start": v(17.53, 73.15) * mm, "mid": v(16.23, 73.45) * mm, "end": v(14.93, 73.73) * mm});
            skArc(sketch, "E22.3.64.0", {"start": v(10.4, 74.5) * mm, "mid": v(9.07, 74.68) * mm, "end": v(7.74, 74.82) * mm});
            skSolve(sketch);
        }
        {
            var Q0;
            Q0=qSketchRegion(id+"F0",true);
            var Q1;
            Q1=makeQuery(id+"F0.imprint","IMPRINT",FACE,{"disambiguationData":[TD([[makeQuery(id+"F0.imprint","IMPRINT",EDGE,{"derivedFrom":sQuery(id+"F0.wireOp",EDGE,"E11")}),-1.0]])]});
            extrude(context, id + "F1", {"entities" : qUnion([Q0, Q1]), "depth" : 6 * mm});
        }
        {
            var Q0;
            Q0=makeQuery(id+"F1.opExtrude","CAP_FACE",FACE,{"disambiguationData":[OSD([sQuery(id+"F0.wireOp",EDGE,"E11"),sQuery(id+"F0.wireOp",EDGE,"E12"),sQuery(id+"F0.wireOp",EDGE,"E13.MirrorCS"),sQuery(id+"F0.wireOp",EDGE,"E14"),sQuery(id+"F0.wireOp",EDGE,"E15.1.0"),sQuery(id+"F0.wireOp",EDGE,"E15.1.1"),sQuery(id+"F0.wireOp",EDGE,"E15.1.2"),sQuery(id+"F0.wireOp",EDGE,"E15.2.0"),sQuery(id+"F0.wireOp",EDGE,"E15.2.1"),sQuery(id+"F0.wireOp",EDGE,"E15.2.2"),sQuery(id+"F0.wireOp",EDGE,"E15.3.0"),sQuery(id+"F0.wireOp",EDGE,"E15.3.1"),sQuery(id+"F0.wireOp",EDGE,"E15.3.2"),sQuery(id+"F0.wireOp",EDGE,"E15.4.0"),sQuery(id+"F0.wireOp",EDGE,"E15.4.1"),sQuery(id+"F0.wireOp",EDGE,"E15.4.2"),sQuery(id+"F0.wireOp",EDGE,"E15.5.0"),sQuery(id+"F0.wireOp",EDGE,"E15.5.1"),sQuery(id+"F0.wireOp",EDGE,"E15.5.2"),sQuery(id+"F0.wireOp",EDGE,"E15.6.0"),sQuery(id+"F0.wireOp",EDGE,"E15.6.1"),sQuery(id+"F0.wireOp",EDGE,"E15.6.2"),sQuery(id+"F0.wireOp",EDGE,"E15.7.0"),sQuery(id+"F0.wireOp",EDGE,"E15.7.1"),sQuery(id+"F0.wireOp",EDGE,"E15.7.2"),sQuery(id+"F0.wireOp",EDGE,"E15.8.0"),sQuery(id+"F0.wireOp",EDGE,"E15.8.1"),sQuery(id+"F0.wireOp",EDGE,"E15.8.2"),sQuery(id+"F0.wireOp",EDGE,"E15.9.0"),sQuery(id+"F0.wireOp",EDGE,"E15.9.1"),sQuery(id+"F0.wireOp",EDGE,"E15.9.2"),sQuery(id+"F0.wireOp",EDGE,"E15.10.0"),sQuery(id+"F0.wireOp",EDGE,"E15.10.1"),sQuery(id+"F0.wireOp",EDGE,"E15.10.2"),sQuery(id+"F0.wireOp",EDGE,"E15.11.0"),sQuery(id+"F0.wireOp",EDGE,"E15.11.1"),sQuery(id+"F0.wireOp",EDGE,"E15.11.2"),sQuery(id+"F0.wireOp",EDGE,"E15.12.0"),sQuery(id+"F0.wireOp",EDGE,"E15.12.1"),sQuery(id+"F0.wireOp",EDGE,"E15.12.2"),sQuery(id+"F0.wireOp",EDGE,"E15.13.0"),sQuery(id+"F0.wireOp",EDGE,"E15.13.1"),sQuery(id+"F0.wireOp",EDGE,"E15.13.2"),sQuery(id+"F0.wireOp",EDGE,"E15.14.0"),sQuery(id+"F0.wireOp",EDGE,"E15.14.1"),sQuery(id+"F0.wireOp",EDGE,"E15.14.2"),sQuery(id+"F0.wireOp",EDGE,"E15.15.0"),sQuery(id+"F0.wireOp",EDGE,"E15.15.1"),sQuery(id+"F0.wireOp",EDGE,"E15.15.2"),sQuery(id+"F0.wireOp",EDGE,"E15.16.0"),sQuery(id+"F0.wireOp",EDGE,"E15.16.1"),sQuery(id+"F0.wireOp",EDGE,"E15.16.2"),sQuery(id+"F0.wireOp",EDGE,"E15.17.0"),sQuery(id+"F0.wireOp",EDGE,"E15.17.1"),sQuery(id+"F0.wireOp",EDGE,"E15.17.2"),sQuery(id+"F0.wireOp",EDGE,"E15.18.0"),sQuery(id+"F0.wireOp",EDGE,"E15.18.1"),sQuery(id+"F0.wireOp",EDGE,"E15.18.2"),sQuery(id+"F0.wireOp",EDGE,"E15.19.0"),sQuery(id+"F0.wireOp",EDGE,"E15.19.1"),sQuery(id+"F0.wireOp",EDGE,"E15.19.2"),sQuery(id+"F0.wireOp",EDGE,"E15.20.0"),sQuery(id+"F0.wireOp",EDGE,"E15.20.1"),sQuery(id+"F0.wireOp",EDGE,"E15.20.2"),sQuery(id+"F0.wireOp",EDGE,"E15.21.0"),sQuery(id+"F0.wireOp",EDGE,"E15.21.1"),sQuery(id+"F0.wireOp",EDGE,"E15.21.2"),sQuery(id+"F0.wireOp",EDGE,"E15.22.0"),sQuery(id+"F0.wireOp",EDGE,"E15.22.1"),sQuery(id+"F0.wireOp",EDGE,"E15.22.2"),sQuery(id+"F0.wireOp",EDGE,"E15.23.0"),sQuery(id+"F0.wireOp",EDGE,"E15.23.1"),sQuery(id+"F0.wireOp",EDGE,"E15.23.2"),sQuery(id+"F0.wireOp",EDGE,"E15.24.0"),sQuery(id+"F0.wireOp",EDGE,"E15.24.1"),sQuery(id+"F0.wireOp",EDGE,"E15.24.2"),sQuery(id+"F0.wireOp",EDGE,"E15.25.0"),sQuery(id+"F0.wireOp",EDGE,"E15.25.1"),sQuery(id+"F0.wireOp",EDGE,"E15.25.2"),sQuery(id+"F0.wireOp",EDGE,"E15.26.0"),sQuery(id+"F0.wireOp",EDGE,"E15.26.1"),sQuery(id+"F0.wireOp",EDGE,"E15.26.2"),sQuery(id+"F0.wireOp",EDGE,"E15.27.0"),sQuery(id+"F0.wireOp",EDGE,"E15.27.1"),sQuery(id+"F0.wireOp",EDGE,"E15.27.2"),sQuery(id+"F0.wireOp",EDGE,"E15.28.0"),sQuery(id+"F0.wireOp",EDGE,"E15.28.1"),sQuery(id+"F0.wireOp",EDGE,"E15.28.2"),sQuery(id+"F0.wireOp",EDGE,"E15.29.0"),sQuery(id+"F0.wireOp",EDGE,"E15.29.1"),sQuery(id+"F0.wireOp",EDGE,"E15.29.2"),sQuery(id+"F0.wireOp",EDGE,"E15.30.0"),sQuery(id+"F0.wireOp",EDGE,"E15.30.1"),sQuery(id+"F0.wireOp",EDGE,"E15.30.2"),sQuery(id+"F0.wireOp",EDGE,"E15.31.0"),sQuery(id+"F0.wireOp",EDGE,"E15.31.1"),sQuery(id+"F0.wireOp",EDGE,"E15.31.2"),sQuery(id+"F0.wireOp",EDGE,"E15.32.0"),sQuery(id+"F0.wireOp",EDGE,"E15.32.1"),sQuery(id+"F0.wireOp",EDGE,"E15.32.2"),sQuery(id+"F0.wireOp",EDGE,"E15.33.0"),sQuery(id+"F0.wireOp",EDGE,"E15.33.1"),sQuery(id+"F0.wireOp",EDGE,"E15.33.2"),sQuery(id+"F0.wireOp",EDGE,"E15.34.0"),sQuery(id+"F0.wireOp",EDGE,"E15.34.1"),sQuery(id+"F0.wireOp",EDGE,"E15.34.2"),sQuery(id+"F0.wireOp",EDGE,"E15.35.0"),sQuery(id+"F0.wireOp",EDGE,"E15.35.1"),sQuery(id+"F0.wireOp",EDGE,"E15.35.2"),sQuery(id+"F0.wireOp",EDGE,"E15.36.0"),sQuery(id+"F0.wireOp",EDGE,"E15.36.1"),sQuery(id+"F0.wireOp",EDGE,"E15.36.2"),sQuery(id+"F0.wireOp",EDGE,"E15.37.0"),sQuery(id+"F0.wireOp",EDGE,"E15.37.1"),sQuery(id+"F0.wireOp",EDGE,"E15.37.2"),sQuery(id+"F0.wireOp",EDGE,"E15.38.0"),sQuery(id+"F0.wireOp",EDGE,"E15.38.1"),sQuery(id+"F0.wireOp",EDGE,"E15.38.2"),sQuery(id+"F0.wireOp",EDGE,"E15.39.0"),sQuery(id+"F0.wireOp",EDGE,"E15.39.1"),sQuery(id+"F0.wireOp",EDGE,"E15.39.2"),sQuery(id+"F0.wireOp",EDGE,"E15.40.0"),sQuery(id+"F0.wireOp",EDGE,"E15.40.1"),sQuery(id+"F0.wireOp",EDGE,"E15.40.2"),sQuery(id+"F0.wireOp",EDGE,"E15.41.0"),sQuery(id+"F0.wireOp",EDGE,"E15.41.1"),sQuery(id+"F0.wireOp",EDGE,"E15.41.2"),sQuery(id+"F0.wireOp",EDGE,"E15.42.0"),sQuery(id+"F0.wireOp",EDGE,"E15.42.1"),sQuery(id+"F0.wireOp",EDGE,"E15.42.2"),sQuery(id+"F0.wireOp",EDGE,"E15.43.0"),sQuery(id+"F0.wireOp",EDGE,"E15.43.1"),sQuery(id+"F0.wireOp",EDGE,"E15.43.2"),sQuery(id+"F0.wireOp",EDGE,"E15.44.0"),sQuery(id+"F0.wireOp",EDGE,"E15.44.1"),sQuery(id+"F0.wireOp",EDGE,"E15.44.2"),sQuery(id+"F0.wireOp",EDGE,"E15.45.0"),sQuery(id+"F0.wireOp",EDGE,"E15.45.1"),sQuery(id+"F0.wireOp",EDGE,"E15.45.2"),sQuery(id+"F0.wireOp",EDGE,"E15.46.0"),sQuery(id+"F0.wireOp",EDGE,"E15.46.1"),sQuery(id+"F0.wireOp",EDGE,"E15.46.2"),sQuery(id+"F0.wireOp",EDGE,"E15.47.0"),sQuery(id+"F0.wireOp",EDGE,"E15.47.1"),sQuery(id+"F0.wireOp",EDGE,"E15.47.2"),sQuery(id+"F0.wireOp",EDGE,"E16.4.48.0"),sQuery(id+"F0.wireOp",EDGE,"E16.8.48.0"),sQuery(id+"F0.wireOp",EDGE,"E16.10.48.0"),sQuery(id+"F0.wireOp",EDGE,"E16.4.49.0"),sQuery(id+"F0.wireOp",EDGE,"E16.8.49.0"),sQuery(id+"F0.wireOp",EDGE,"E16.10.49.0"),sQuery(id+"F0.wireOp",EDGE,"E17"),sQuery(id+"F0.wireOp",EDGE,"E18.1.0"),sQuery(id+"F0.wireOp",EDGE,"E18.2.0"),sQuery(id+"F0.wireOp",EDGE,"E18.3.0"),sQuery(id+"F0.wireOp",EDGE,"E18.4.0"),sQuery(id+"F0.wireOp",EDGE,"E18.5.0"),sQuery(id+"F0.wireOp",EDGE,"E18.6.0"),sQuery(id+"F0.wireOp",EDGE,"E18.7.0"),sQuery(id+"F0.wireOp",EDGE,"E18.8.0"),sQuery(id+"F0.wireOp",EDGE,"E18.9.0"),sQuery(id+"F0.wireOp",EDGE,"E18.10.0"),sQuery(id+"F0.wireOp",EDGE,"E18.11.0"),sQuery(id+"F0.wireOp",EDGE,"E18.12.0"),sQuery(id+"F0.wireOp",EDGE,"E18.13.0"),sQuery(id+"F0.wireOp",EDGE,"E18.14.0"),sQuery(id+"F0.wireOp",EDGE,"E18.15.0"),sQuery(id+"F0.wireOp",EDGE,"E18.16.0"),sQuery(id+"F0.wireOp",EDGE,"E18.17.0"),sQuery(id+"F0.wireOp",EDGE,"E18.18.0"),sQuery(id+"F0.wireOp",EDGE,"E18.19.0"),sQuery(id+"F0.wireOp",EDGE,"E18.20.0"),sQuery(id+"F0.wireOp",EDGE,"E18.21.0"),sQuery(id+"F0.wireOp",EDGE,"E18.22.0"),sQuery(id+"F0.wireOp",EDGE,"E18.23.0"),sQuery(id+"F0.wireOp",EDGE,"E18.24.0"),sQuery(id+"F0.wireOp",EDGE,"E18.25.0"),sQuery(id+"F0.wireOp",EDGE,"E18.26.0"),sQuery(id+"F0.wireOp",EDGE,"E18.27.0"),sQuery(id+"F0.wireOp",EDGE,"E18.28.0"),sQuery(id+"F0.wireOp",EDGE,"E18.29.0"),sQuery(id+"F0.wireOp",EDGE,"E18.30.0"),sQuery(id+"F0.wireOp",EDGE,"E18.31.0"),sQuery(id+"F0.wireOp",EDGE,"E18.32.0"),sQuery(id+"F0.wireOp",EDGE,"E18.33.0"),sQuery(id+"F0.wireOp",EDGE,"E18.34.0"),sQuery(id+"F0.wireOp",EDGE,"E18.35.0"),sQuery(id+"F0.wireOp",EDGE,"E18.36.0"),sQuery(id+"F0.wireOp",EDGE,"E18.37.0"),sQuery(id+"F0.wireOp",EDGE,"E18.38.0"),sQuery(id+"F0.wireOp",EDGE,"E18.39.0"),sQuery(id+"F0.wireOp",EDGE,"E18.40.0"),sQuery(id+"F0.wireOp",EDGE,"E18.41.0"),sQuery(id+"F0.wireOp",EDGE,"E18.42.0"),sQuery(id+"F0.wireOp",EDGE,"E18.43.0"),sQuery(id+"F0.wireOp",EDGE,"E18.44.0"),sQuery(id+"F0.wireOp",EDGE,"E18.45.0"),sQuery(id+"F0.wireOp",EDGE,"E18.46.0"),sQuery(id+"F0.wireOp",EDGE,"E18.47.0"),sQuery(id+"F0.wireOp",EDGE,"E18.48.0"),sQuery(id+"F0.wireOp",EDGE,"E18.49.0"),sQuery(id+"F0.wireOp",EDGE,"E19.4.50.0"),sQuery(id+"F0.wireOp",EDGE,"E19.8.50.0"),sQuery(id+"F0.wireOp",EDGE,"E19.10.50.0"),sQuery(id+"F0.wireOp",EDGE,"E20.3.50.0"),sQuery(id+"F0.wireOp",EDGE,"E21.4.51.0"),sQuery(id+"F0.wireOp",EDGE,"E21.8.51.0"),sQuery(id+"F0.wireOp",EDGE,"E21.10.51.0"),sQuery(id+"F0.wireOp",EDGE,"E21.4.52.0"),sQuery(id+"F0.wireOp",EDGE,"E21.8.52.0"),sQuery(id+"F0.wireOp",EDGE,"E21.10.52.0"),sQuery(id+"F0.wireOp",EDGE,"E21.4.53.0"),sQuery(id+"F0.wireOp",EDGE,"E21.8.53.0"),sQuery(id+"F0.wireOp",EDGE,"E21.10.53.0"),sQuery(id+"F0.wireOp",EDGE,"E21.4.54.0"),sQuery(id+"F0.wireOp",EDGE,"E21.8.54.0"),sQuery(id+"F0.wireOp",EDGE,"E21.10.54.0"),sQuery(id+"F0.wireOp",EDGE,"E21.4.55.0"),sQuery(id+"F0.wireOp",EDGE,"E21.8.55.0"),sQuery(id+"F0.wireOp",EDGE,"E21.10.55.0"),sQuery(id+"F0.wireOp",EDGE,"E21.4.56.0"),sQuery(id+"F0.wireOp",EDGE,"E21.8.56.0"),sQuery(id+"F0.wireOp",EDGE,"E21.10.56.0"),sQuery(id+"F0.wireOp",EDGE,"E21.4.57.0"),sQuery(id+"F0.wireOp",EDGE,"E21.8.57.0"),sQuery(id+"F0.wireOp",EDGE,"E21.10.57.0"),sQuery(id+"F0.wireOp",EDGE,"E21.4.58.0"),sQuery(id+"F0.wireOp",EDGE,"E21.8.58.0"),sQuery(id+"F0.wireOp",EDGE,"E21.10.58.0"),sQuery(id+"F0.wireOp",EDGE,"E21.4.59.0"),sQuery(id+"F0.wireOp",EDGE,"E21.8.59.0"),sQuery(id+"F0.wireOp",EDGE,"E21.10.59.0"),sQuery(id+"F0.wireOp",EDGE,"E21.4.60.0"),sQuery(id+"F0.wireOp",EDGE,"E21.8.60.0"),sQuery(id+"F0.wireOp",EDGE,"E21.10.60.0"),sQuery(id+"F0.wireOp",EDGE,"E21.4.61.0"),sQuery(id+"F0.wireOp",EDGE,"E21.8.61.0"),sQuery(id+"F0.wireOp",EDGE,"E21.10.61.0"),sQuery(id+"F0.wireOp",EDGE,"E21.4.62.0"),sQuery(id+"F0.wireOp",EDGE,"E21.8.62.0"),sQuery(id+"F0.wireOp",EDGE,"E21.10.62.0"),sQuery(id+"F0.wireOp",EDGE,"E21.4.63.0"),sQuery(id+"F0.wireOp",EDGE,"E21.8.63.0"),sQuery(id+"F0.wireOp",EDGE,"E21.10.63.0"),sQuery(id+"F0.wireOp",EDGE,"E21.4.64.0"),sQuery(id+"F0.wireOp",EDGE,"E21.8.64.0"),sQuery(id+"F0.wireOp",EDGE,"E21.10.64.0"),sQuery(id+"F0.wireOp",EDGE,"E22.3.51.0"),sQuery(id+"F0.wireOp",EDGE,"E22.3.52.0"),sQuery(id+"F0.wireOp",EDGE,"E22.3.53.0"),sQuery(id+"F0.wireOp",EDGE,"E22.3.54.0"),sQuery(id+"F0.wireOp",EDGE,"E22.3.55.0"),sQuery(id+"F0.wireOp",EDGE,"E22.3.56.0"),sQuery(id+"F0.wireOp",EDGE,"E22.3.57.0"),sQuery(id+"F0.wireOp",EDGE,"E22.3.58.0"),sQuery(id+"F0.wireOp",EDGE,"E22.3.59.0"),sQuery(id+"F0.wireOp",EDGE,"E22.3.60.0"),sQuery(id+"F0.wireOp",EDGE,"E22.3.61.0"),sQuery(id+"F0.wireOp",EDGE,"E22.3.62.0"),sQuery(id+"F0.wireOp",EDGE,"E22.3.63.0"),sQuery(id+"F0.wireOp",EDGE,"E22.3.64.0")])],"isStart":false});
            var sketch = newSketch(context, id + "F2", { "sketchPlane" : qUnion([Q0])});
            skCircle(sketch, "E23", {"center": v(50, 0) * mm, "radius": 4.5 * mm});
            skCircle(sketch, "E24", {"center": v(0, 0) * mm, "radius": 12.5 * mm});
            skLineSegment(sketch, "E25", {"start": v(0, 0) * mm, "end": v(64.01, 11.29) * mm, "construction": true});
            skLineSegment(sketch, "E26", {"start": v(0, 0) * mm, "end": v(-22.23, 61.08) * mm, "construction": true});
            skArc(sketch, "E27", {"start": v(64.01, 11.29) * mm, "mid": v(32.5, 56.3) * mm, "end": v(-22.23, 61.08) * mm});
            skLineSegment(sketch, "E28", {"start": v(-22.23, 61.08) * mm, "end": v(-4.28, 11.75) * mm});
            skLineSegment(sketch, "E29", {"start": v(12.31, 2.17) * mm, "end": v(64.01, 11.29) * mm});
            skLineSegment(sketch, "E30", {"start": v(0, 0) * mm, "end": v(65, 0) * mm, "construction": true});
            skLineSegment(sketch, "E31.1.0", {"start": v(-41.78, -49.8) * mm, "end": v(-8.03, -9.58) * mm});
            skLineSegment(sketch, "E31.1.1", {"start": v(-8.03, 9.58) * mm, "end": v(-41.78, 49.8) * mm});
            skArc(sketch, "E31.1.2", {"start": v(-41.78, 49.8) * mm, "mid": v(-65, 0) * mm, "end": v(-41.78, -49.8) * mm});
            skLineSegment(sketch, "E31.2.0", {"start": v(64.01, -11.29) * mm, "end": v(12.31, -2.17) * mm});
            skLineSegment(sketch, "E31.2.1", {"start": v(-4.28, -11.75) * mm, "end": v(-22.23, -61.08) * mm});
            skArc(sketch, "E31.2.2", {"start": v(-22.23, -61.08) * mm, "mid": v(32.5, -56.3) * mm, "end": v(64.01, -11.29) * mm});
            skSolve(sketch);
        }
        {
            var Q0;
            Q0=makeQuery(id+"F2.imprint","IMPRINT",FACE,{"disambiguationData":[TD([[makeQuery(id+"F2.imprint","IMPRINT",EDGE,{"derivedFrom":sQuery(id+"F2.wireOp",EDGE,"E23")}),1.0]])]});
            var Q1;
            {var subQ0=sQuery(id+"F2.wireOp",EDGE,"E31.2.0");Q1=makeQuery(id+"F2.imprint","IMPRINT",FACE,{"disambiguationData":[TD([[makeQuery(id+"F2.imprint","IMPRINT",EDGE,{"derivedFrom":subQ0}),1.0]])]});}
            var Q2;
            {var subQ0=sQuery(id+"F2.wireOp",EDGE,"E31.1.0");Q2=makeQuery(id+"F2.imprint","IMPRINT",FACE,{"disambiguationData":[TD([[makeQuery(id+"F2.imprint","IMPRINT",EDGE,{"derivedFrom":subQ0}),1.0]])]});}
            var Q3;
            Q3=makeQuery(id+"F2.imprint","IMPRINT",FACE,{"disambiguationData":[TD([[makeQuery(id+"F2.imprint","IMPRINT",EDGE,{"derivedFrom":sQuery(id+"F2.wireOp",EDGE,"E27")}),1.0]])]});
            extrude(context, id + "F3", {"entities" : qUnion([Q0, Q1, Q2, Q3]), "operationType" : NewBodyOperationType.REMOVE, "oppositeDirection" : true, "depth" : 25 * mm});
        }
    });
